# Revit family: Table-Teknion-HTMS-upStage_Square_Table-R2022
name_source: partatom
category: Furniture
units: mm (PartAtom-declared; Revit-internal decimal feet)

## family parameters
Always vertical = Yes
Cut with Voids When Loaded = No
OmniClass Number = 23.40.20.00
OmniClass Title = General Furniture and Specialties
Render Appearance Source = Family Geometry
Room Calculation Point = No
Shared = Yes
Work Plane-Based = No

## types (2) — shared parameters
Assembly Code = E2020200
Manufacturer = Teknion
Manufacturer Fax = 416.661.4586
Part Number = HTMS
Product Documentation Link = https://www.teknion.com
Product Line = Meeting Tables
Product Page URL = https://www.teknion.com
Series = upStage
Sustainability Data = https://www.teknion.com
URL = www.teknion.com
Unit Weight URL = http://www.teknion.com
Warranty = http://www.teknion.com
zero-valued in all types: Default Elevation

## per-type parameters (varying)
| type | Description | Model |
| Metal & Metal Base | upStage Square Meeting Table, Metal & Metal Base | HTMSM___ |
| Metal & Wood Base | upStage Square Meeting Table, Metal & Wood Base | HTMSW___ |

## geometry (parser evidence)
native form markers: Sweep x14
no freeform markers — native parametric forms only
